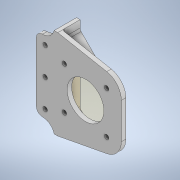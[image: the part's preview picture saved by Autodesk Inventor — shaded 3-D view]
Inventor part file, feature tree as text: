
AUTODESK INVENTOR PART (.ipt)
format: ipt  version: 2021.3 (Build 253353000, 353)  size: 260,608 bytes
history: native  units: mm
features: reference x9, extrude x5, other x4, plane x3, sketch x2, fillet x1
ambient origin geometry x8: Origin, YZ Plane, XZ Plane, XY Plane, X Axis, Y Axis, Z Axis, Center Point
bodies: Solid1 (feature_tree)
feature tree (24):
  plane  "Work Plane1"
  extrude  "Extrusion1"  Depth=10.0mm
  sketch  "Sketch9"  dims[d3=20.0mm d7=10.0mm d8=5.0mm d9=0.0mm d22=10.0mm d23=5.0mm d24=5.0mm d25=5.0mm d26=7.0mm d27=7.0mm d28=20.0mm d29=20.0mm d30=0.5mm d37=4.0mm d38=10.0mm d39=31.0mm d40=31.0mm d42=4.0mm d43=4.0mm d44=4.0mm d45=4.0mm d46=20.0mm d47=40.0mm d48=10.0mm d49=0.0mm d50=10.0mm d51=0.0mm d52=90.0deg d53=90.0deg d54=4.0mm d55=0.0mm d56=4.0mm d57=0.0mm d58=2.0mm d33=0.5mm d34=0.872665mm d35=0.5mm d36=0.872665mm]
  extrude  "Extrusion5"  Depth=10.0mm
  extrude  "Extrusion6"  Depth=2.0mm TaperAngle=0.0deg
  plane  "Work Plane2"
  plane  "Work Plane3"
  extrude  "Extrusion7"  Depth=10.0mm
  extrude  "Extrusion8"  Depth=2.0mm
  fillet  "Fillet2"  Radius=5.0mm
  sketch  "Sketch1"  dims[d1=10.0mm d2=5.0mm]
  reference  "Reference1"
  reference  "Reference2"
  reference  "Reference3"
  reference  "Reference4"
  reference  "Reference5"
  reference  "Reference6"
  reference  "Reference7"
  reference  "Reference8"
  reference  "Reference9"
  other  "<userpath>\Desktop\mechanical_cleaned\custom_parts\drivetrain\motor assembly.iam"
  other  "motor assembly.iam"
  other  "Gearbox:1"
  other  "<userpath>\OneDrive - NXP\ROSinante\Mechanical\Frame Parts\motor assembly.iam"
